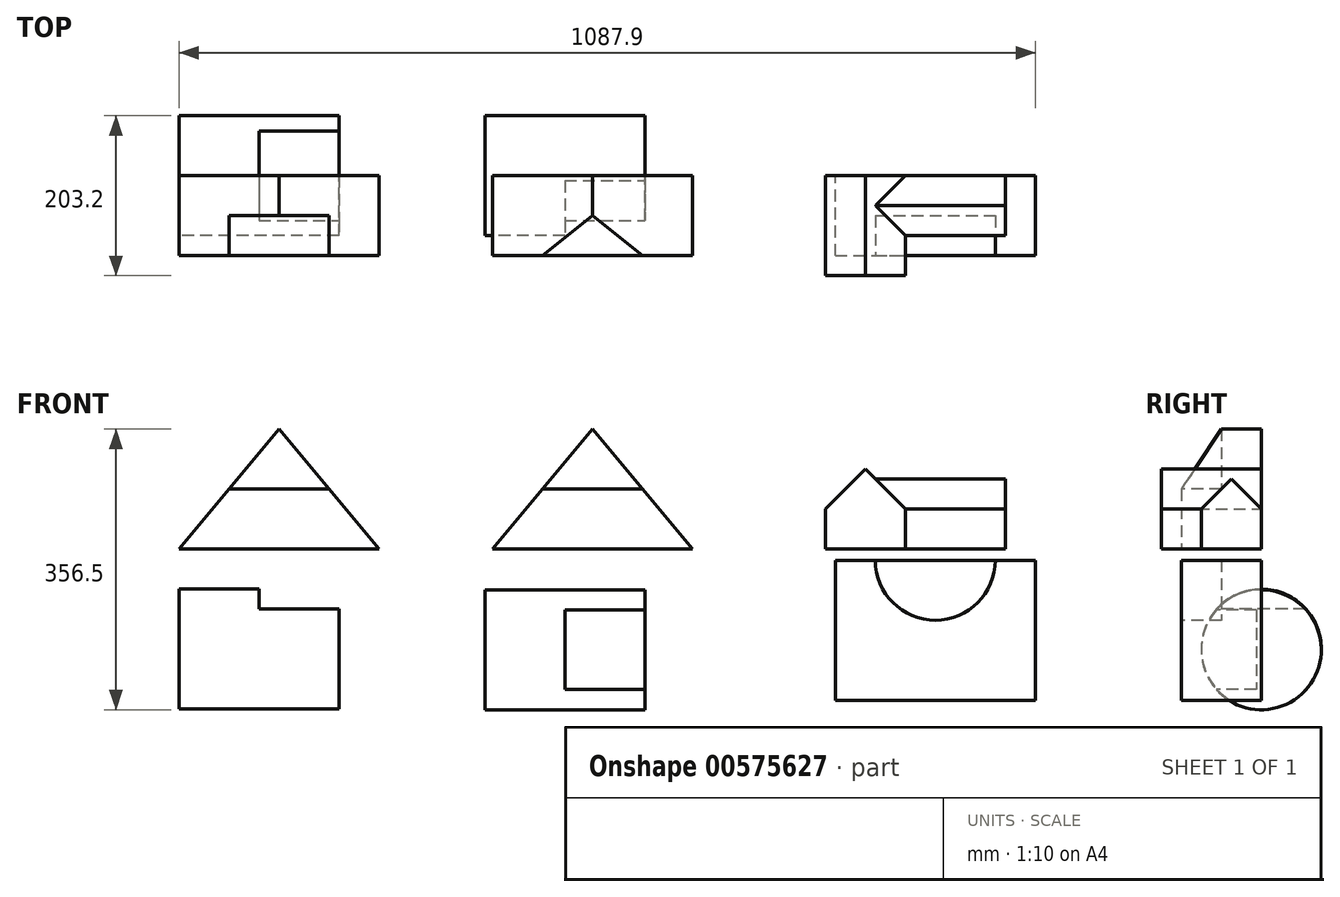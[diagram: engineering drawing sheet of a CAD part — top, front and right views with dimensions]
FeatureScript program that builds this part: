
annotation { "Feature Type Name" : "Feature", "Feature Type Description" : "" }
export const myFeature = defineFeature(function(context is Context, id is Id, definition is map)
    precondition{}
    {
        {
            var Q0;
            Q0=qCreatedBy(makeId("Front.planeOp"),FACE);
            var sketch = newSketch(context, id + "F0", { "sketchPlane" : qUnion([Q0])});
            skLineSegment(sketch, "E0", {"start": v(0, 0) * mm, "end": v(254, 0) * mm});
            skLineSegment(sketch, "E1", {"start": v(127, 152.4) * mm, "end": v(0, 0) * mm});
            skLineSegment(sketch, "E2", {"start": v(127, 152.4) * mm, "end": v(254, 0) * mm});
            skLineSegment(sketch, "E3", {"start": v(127, 76.2) * mm, "end": v(63.5, 76.2) * mm});
            skLineSegment(sketch, "E4", {"start": v(127, 76.2) * mm, "end": v(190.5, 76.2) * mm});
            skSolve(sketch);
        }
        {
            var Q0;
            Q0 = qSketchRegion(id + "F0", true);
            extrude(context, id + "F1", {"entities" : qUnion([Q0]), "depth" : 101.6 * mm, "offsetDistance" : 25.4 * mm});
        }
        {
            var Q0;
            Q0=makeQuery(id+"F1.opExtrude","CAP_FACE",FACE,{"disambiguationData":[OSD([sQuery(id+"F0.wireOp",EDGE,"E0"),sQuery(id+"F0.wireOp",EDGE,"E1"),sQuery(id+"F0.wireOp",EDGE,"E2")])],"isStart":false});
            var sketch = newSketch(context, id + "F2", { "sketchPlane" : qUnion([Q0])});
            skLineSegment(sketch, "E5", {"start": v(127, 76.2) * mm, "end": v(190.5, 76.2) * mm});
            skLineSegment(sketch, "E6", {"start": v(127, 76.2) * mm, "end": v(63.5, 76.2) * mm});
            skSolve(sketch);
        }
        {
            var Q0;
            {var subQ0=sQuery(id+"F2.wireOp",EDGE,"E5");Q0=makeQuery(id+"F2.imprint","IMPRINT",FACE,{"disambiguationData":[TD([[makeQuery(id+"F2.imprint","IMPRINT",EDGE,{"derivedFrom":subQ0}),1.0]])]});}
            extrude(context, id + "F3", {"entities" : qUnion([Q0]), "operationType" : NewBodyOperationType.REMOVE, "oppositeDirection" : true, "depth" : 50.8 * mm, "offsetDistance" : 25.4 * mm});
        }
        {
            var Q0;
            Q0=qCreatedBy(makeId("Front.planeOp"),FACE);
            var sketch = newSketch(context, id + "F4", { "sketchPlane" : qUnion([Q0])});
            skLineSegment(sketch, "E7", {"start": v(398.21, 0) * mm, "end": v(652.21, 0) * mm});
            skLineSegment(sketch, "E8", {"start": v(525.21, 152.4) * mm, "end": v(398.21, 0) * mm});
            skLineSegment(sketch, "E9", {"start": v(525.21, 152.4) * mm, "end": v(652.21, 0) * mm});
            skSolve(sketch);
        }
        {
            var Q0;
            Q0 = qSketchRegion(id + "F4", true);
            extrude(context, id + "F5", {"entities" : qUnion([Q0]), "depth" : 101.6 * mm, "offsetDistance" : 25.4 * mm});
        }
        {
            var Q0;
            Q0=makeQuery(id+"F5.opExtrude","SWEPT_FACE",FACE,{"disambiguationData":[OSD([sQuery(id+"F4.wireOp",EDGE,"E9")])]});
            var sketch = newSketch(context, id + "F6", { "sketchPlane" : qUnion([Q0])});
            skLineSegment(sketch, "E10", {"start": v(-101.6, -318.34) * mm, "end": v(0, -318.34) * mm});
            skLineSegment(sketch, "E11", {"start": v(0, -219.15) * mm, "end": v(-50.8, -219.15) * mm});
            skLineSegment(sketch, "E12", {"start": v(-101.6, -318.34) * mm, "end": v(-50.8, -219.15) * mm});
            skSolve(sketch);
        }
        {
            var Q0;
            {var subQ0=sQuery(id+"F6.wireOp",EDGE,"E12");Q0=makeQuery(id+"F6.imprint","IMPRINT",FACE,{"disambiguationData":[TD([[makeQuery(id+"F6.imprint","IMPRINT",EDGE,{"derivedFrom":subQ0}),1.0]])]});}
            extrude(context, id + "F7", {"entities" : qUnion([Q0]), "operationType" : NewBodyOperationType.REMOVE, "depth" : 101.6 * mm, "offsetDistance" : 25.4 * mm});
        }
        {
            var Q0;
            Q0=makeQuery(id+"F5.opExtrude","CAP_EDGE",EDGE,{"disambiguationData":[OSD([sQuery(id+"F4.wireOp",EDGE,"E7")])],"isStart":false});
            cPoint(context, id + "F8", {"entities" : qUnion([Q0]), "parameter" : 0.5});
        }
        {
            var Q0;
            Q0=makeQuery(id+"F5.opExtrude","CAP_VERTEX",VERTEX,{"disambiguationData":[OSD([sQuery(id+"F4.wireOp",EDGE,"E8"),sQuery(id+"F4.wireOp",EDGE,"E9")])],"isStart":false});
            var Q1;
            Q1=makeQuery(id+"F5.opExtrude","CAP_VERTEX",VERTEX,{"disambiguationData":[OSD([sQuery(id+"F4.wireOp",EDGE,"E8"),sQuery(id+"F4.wireOp",EDGE,"E9")])],"isStart":true});
            var Q2;
            Q2 = qCreatedBy(id + "F8" ,VERTEX);
            cPlane(context, id + "F9", {"entities" : qUnion([Q0, Q1, Q2]), "cplaneType" : CPlaneType.THREE_POINT, "offset" : 25.4 * mm, "width" : 152.4 * mm, "height" : 152.4 * mm});
        }
        {
            var Q0;
            Q0=qCreatedBy(id+"F9.planeOp",FACE);
            var sketch = newSketch(context, id + "F10", { "sketchPlane" : qUnion([Q0])});
            skLineSegment(sketch, "E13", {"start": v(-101.6, 152.4) * mm, "end": v(-50.8, 152.4) * mm});
            skLineSegment(sketch, "E14", {"start": v(-101.6, 152.4) * mm, "end": v(-101.6, 76.2) * mm});
            skLineSegment(sketch, "E15", {"start": v(-101.6, 76.2) * mm, "end": v(-50.8, 152.4) * mm});
            skSolve(sketch);
        }
        {
            var Q0;
            Q0 = qSketchRegion(id + "F10", true);
            extrude(context, id + "F11", {"entities" : qUnion([Q0]), "operationType" : NewBodyOperationType.REMOVE, "endBound" : BoundingType.SYMMETRIC, "depth" : 127 * mm, "offsetDistance" : 25.4 * mm});
        }
        {
            var Q0;
            Q0=qCreatedBy(makeId("Front.planeOp"),FACE);
            var sketch = newSketch(context, id + "F12", { "sketchPlane" : qUnion([Q0])});
            skLineSegment(sketch, "E16", {"start": v(923, 0) * mm, "end": v(821.4, 0) * mm});
            skLineSegment(sketch, "E17", {"start": v(923, 0) * mm, "end": v(923, 50.8) * mm});
            skLineSegment(sketch, "E18", {"start": v(821.4, 0) * mm, "end": v(821.4, 50.8) * mm});
            skLineSegment(sketch, "E19", {"start": v(872.2, 101.6) * mm, "end": v(821.4, 50.8) * mm});
            skLineSegment(sketch, "E20", {"start": v(872.2, 101.6) * mm, "end": v(923, 50.8) * mm});
            skLineSegment(sketch, "E21", {"start": v(923, 0) * mm, "end": v(1050, 0) * mm});
            skLineSegment(sketch, "E22", {"start": v(1050, 0) * mm, "end": v(1050, 50.8) * mm});
            skLineSegment(sketch, "E23", {"start": v(1050, 50.8) * mm, "end": v(923, 50.8) * mm});
            skSolve(sketch);
        }
        {
            var Q0;
            Q0=makeQuery(id+"F12.imprint","IMPRINT",FACE,{"disambiguationData":[TD([[makeQuery(id+"F12.imprint","IMPRINT",EDGE,{"derivedFrom":sQuery(id+"F12.wireOp",EDGE,"E16")}),-1.0]])]});
            var Q1;
            Q1=makeQuery(id+"F12.imprint","IMPRINT",FACE,{"disambiguationData":[TD([[makeQuery(id+"F12.imprint","IMPRINT",EDGE,{"derivedFrom":sQuery(id+"F12.wireOp",EDGE,"E17")}),-1.0]])]});
            extrude(context, id + "F13", {"entities" : qUnion([Q0, Q1]), "depth" : 127 * mm, "offsetDistance" : 25.4 * mm});
        }
        {
            var Q0;
            Q0=makeQuery(id+"F13.opExtrude","SWEPT_FACE",FACE,{"disambiguationData":[OSD([sQuery(id+"F12.wireOp",EDGE,"E22")])]});
            var sketch = newSketch(context, id + "F14", { "sketchPlane" : qUnion([Q0])});
            skLineSegment(sketch, "E24.bottom", {"start": v(-127, 50.8) * mm, "end": v(-76.2, 50.8) * mm});
            skLineSegment(sketch, "E24.top", {"start": v(-127, 0) * mm, "end": v(-76.2, 0) * mm});
            skLineSegment(sketch, "E24.left", {"start": v(-127, 50.8) * mm, "end": v(-127, 0) * mm});
            skLineSegment(sketch, "E24.right", {"start": v(-76.2, 50.8) * mm, "end": v(-76.2, 0) * mm});
            skLineSegment(sketch, "E25", {"start": v(-76.2, 0) * mm, "end": v(0, 0) * mm});
            skLineSegment(sketch, "E26", {"start": v(-38.1, 88.9) * mm, "end": v(-76.2, 50.8) * mm});
            skLineSegment(sketch, "E27", {"start": v(-38.1, 88.9) * mm, "end": v(0, 50.8) * mm});
            skLineSegment(sketch, "E28", {"start": v(-127, 50.8) * mm, "end": v(-127, 88.44) * mm});
            skLineSegment(sketch, "E29", {"start": v(-127, 88.44) * mm, "end": v(-38.1, 88.9) * mm});
            skLineSegment(sketch, "E30", {"start": v(-38.1, 88.9) * mm, "end": v(0, 89.1) * mm});
            skSolve(sketch);
        }
        {
            var Q0;
            {var subQ0=sQuery(id+"F14.wireOp",EDGE,"E26");Q0=makeQuery(id+"F14.imprint","IMPRINT",FACE,{"disambiguationData":[TD([[makeQuery(id+"F14.imprint","IMPRINT",EDGE,{"derivedFrom":subQ0}),1.0]])]});}
            extrude(context, id + "F15", {"entities" : qUnion([Q0]), "operationType" : NewBodyOperationType.ADD, "oppositeDirection" : true, "depth" : 164.34 * mm, "offsetDistance" : 25.4 * mm});
        }
        {
            var Q0;
            Q0=makeQuery(id+"F13.opExtrude","CAP_FACE",FACE,{"disambiguationData":[OSD([sQuery(id+"F12.wireOp",EDGE,"E16"),sQuery(id+"F12.wireOp",EDGE,"E18"),sQuery(id+"F12.wireOp",EDGE,"E19"),sQuery(id+"F12.wireOp",EDGE,"E20"),sQuery(id+"F12.wireOp",EDGE,"E21"),sQuery(id+"F12.wireOp",EDGE,"E22"),sQuery(id+"F12.wireOp",EDGE,"E23")])],"isStart":false});
            var sketch = newSketch(context, id + "F16", { "sketchPlane" : qUnion([Q0])});
            skLineSegment(sketch, "E31.bottom", {"start": v(1050, 0) * mm, "end": v(923, 0) * mm});
            skLineSegment(sketch, "E31.top", {"start": v(1050, 50.8) * mm, "end": v(923, 50.8) * mm});
            skLineSegment(sketch, "E31.left", {"start": v(1050, 0) * mm, "end": v(1050, 50.8) * mm});
            skLineSegment(sketch, "E31.right", {"start": v(923, 0) * mm, "end": v(923, 50.8) * mm});
            skSolve(sketch);
        }
        {
            var Q0;
            Q0=makeQuery(id+"F16.imprint","IMPRINT",FACE,{"disambiguationData":[TD([[makeQuery(id+"F16.imprint","IMPRINT",EDGE,{"derivedFrom":sQuery(id+"F16.wireOp",EDGE,"E31.bottom")}),-1.0]])]});
            extrude(context, id + "F17", {"entities" : qUnion([Q0]), "operationType" : NewBodyOperationType.REMOVE, "oppositeDirection" : true, "depth" : 50.8 * mm, "offsetDistance" : 25.4 * mm});
        }
        {
            var Q0;
            Q0=qCreatedBy(makeId("Right.planeOp"),FACE);
            var sketch = newSketch(context, id + "F18", { "sketchPlane" : qUnion([Q0])});
            skCircle(sketch, "E32", {"center": v(0, -127) * mm, "radius": 76.2 * mm});
            skSolve(sketch);
        }
        {
            var Q0;
            Q0 = qSketchRegion(id + "F18", true);
            extrude(context, id + "F19", {"entities" : qUnion([Q0]), "depth" : 203.2 * mm, "offsetDistance" : 25.4 * mm});
        }
        {
            var Q0;
            Q0=makeQuery(id+"F19.opExtrude","CAP_FACE",FACE,{"disambiguationData":[OSD([sQuery(id+"F18.wireOp",EDGE,"E32")])],"isStart":false});
            var sketch = newSketch(context, id + "F20", { "sketchPlane" : qUnion([Q0])});
            skLineSegment(sketch, "E33", {"start": v(0, -203.2) * mm, "end": v(0, -76.2) * mm});
            skLineSegment(sketch, "E34", {"start": v(0, -76.2) * mm, "end": v(56.8, -76.2) * mm});
            skLineSegment(sketch, "E35", {"start": v(0, -76.2) * mm, "end": v(-56.8, -76.2) * mm});
            skLineSegment(sketch, "E36", {"start": v(0, -76.2) * mm, "end": v(0, -50.8) * mm});
            skSolve(sketch);
        }
        {
            var Q0;
            {var subQ0=sQuery(id+"F20.wireOp",EDGE,"E35");Q0=makeQuery(id+"F20.imprint","IMPRINT",FACE,{"disambiguationData":[TD([[makeQuery(id+"F20.imprint","IMPRINT",EDGE,{"derivedFrom":subQ0}),-1.0]])]});}
            var Q1;
            {var subQ0=sQuery(id+"F20.wireOp",EDGE,"E34");Q1=makeQuery(id+"F20.imprint","IMPRINT",FACE,{"disambiguationData":[TD([[makeQuery(id+"F20.imprint","IMPRINT",EDGE,{"derivedFrom":subQ0}),1.0]])]});}
            extrude(context, id + "F21", {"entities" : qUnion([Q0, Q1]), "operationType" : NewBodyOperationType.REMOVE, "oppositeDirection" : true, "depth" : 101.6 * mm, "offsetDistance" : 25.4 * mm});
        }
        {
            var Q0;
            Q0=qCreatedBy(makeId("Right.planeOp"),FACE);
            cPlane(context, id + "F22", {"entities" : qUnion([Q0]), "cplaneType" : CPlaneType.OFFSET, "offset" : 388.62 * mm, "width" : 152.4 * mm, "height" : 152.4 * mm});
        }
        {
            var Q0;
            Q0=qCreatedBy(id+"F22.planeOp",FACE);
            var sketch = newSketch(context, id + "F23", { "sketchPlane" : qUnion([Q0])});
            skCircle(sketch, "E37", {"center": v(0, -127.9) * mm, "radius": 76.2 * mm});
            skSolve(sketch);
        }
        {
            var Q0;
            Q0 = qSketchRegion(id + "F23", true);
            extrude(context, id + "F24", {"entities" : qUnion([Q0]), "depth" : 203.2 * mm, "offsetDistance" : 25.4 * mm});
        }
        {
            var Q0;
            Q0=makeQuery(id+"F24.opExtrude","CAP_FACE",FACE,{"disambiguationData":[OSD([sQuery(id+"F23.wireOp",EDGE,"E37")])],"isStart":false});
            var sketch = newSketch(context, id + "F25", { "sketchPlane" : qUnion([Q0])});
            skLineSegment(sketch, "E38", {"start": v(-6.22, -203.85) * mm, "end": v(-6.22, -178.45) * mm});
            skLineSegment(sketch, "E39", {"start": v(-6.22, -178.45) * mm, "end": v(-57.02, -178.45) * mm});
            skLineSegment(sketch, "E40", {"start": v(-6.22, -51.96) * mm, "end": v(-6.22, -77.36) * mm});
            skLineSegment(sketch, "E41", {"start": v(-6.22, -77.36) * mm, "end": v(-57.02, -77.36) * mm});
            skLineSegment(sketch, "E42", {"start": v(-6.22, -77.36) * mm, "end": v(-6.22, -178.45) * mm});
            skSolve(sketch);
        }
        {
            var Q0;
            {var subQ0=sQuery(id+"F25.wireOp",EDGE,"E39");Q0=makeQuery(id+"F25.imprint","IMPRINT",FACE,{"disambiguationData":[TD([[makeQuery(id+"F25.imprint","IMPRINT",EDGE,{"derivedFrom":subQ0}),-1.0]])]});}
            extrude(context, id + "F26", {"entities" : qUnion([Q0]), "operationType" : NewBodyOperationType.REMOVE, "oppositeDirection" : true, "depth" : 101.6 * mm, "offsetDistance" : 25.4 * mm});
        }
        {
            var Q0;
            Q0=qCreatedBy(makeId("Front.planeOp"),FACE);
            var sketch = newSketch(context, id + "F27", { "sketchPlane" : qUnion([Q0])});
            skLineSegment(sketch, "E43", {"start": v(833.9, -191.92) * mm, "end": v(1087.9, -191.92) * mm});
            skLineSegment(sketch, "E44", {"start": v(1087.9, -191.92) * mm, "end": v(1087.9, -14.12) * mm});
            skLineSegment(sketch, "E45", {"start": v(833.9, -191.92) * mm, "end": v(833.9, -14.12) * mm});
            skLineSegment(sketch, "E46", {"start": v(833.9, -14.12) * mm, "end": v(1087.9, -14.12) * mm});
            skSolve(sketch);
        }
        {
            var Q0;
            Q0=makeQuery(id+"F27.imprint","IMPRINT",FACE,{"disambiguationData":[TD([[makeQuery(id+"F27.imprint","IMPRINT",EDGE,{"derivedFrom":sQuery(id+"F27.wireOp",EDGE,"E43")}),1.0]])]});
            extrude(context, id + "F28", {"entities" : qUnion([Q0]), "depth" : 101.6 * mm, "offsetDistance" : 25.4 * mm});
        }
        {
            var Q0;
            Q0=makeQuery(id+"F28.opExtrude","CAP_FACE",FACE,{"disambiguationData":[OSD([sQuery(id+"F27.wireOp",EDGE,"E43"),sQuery(id+"F27.wireOp",EDGE,"E44"),sQuery(id+"F27.wireOp",EDGE,"E45"),sQuery(id+"F27.wireOp",EDGE,"E46")])],"isStart":false});
            var sketch = newSketch(context, id + "F29", { "sketchPlane" : qUnion([Q0])});
            skCircle(sketch, "E47", {"center": v(960.9, -14.12) * mm, "radius": 76.2 * mm});
            skSolve(sketch);
        }
        {
            var Q0;
            {var subQ0=sQuery(id+"F29.wireOp",EDGE,"E47");var subQ1=makeQuery(id+"F28.opExtrude","CAP_EDGE",EDGE,{"disambiguationData":[OSD([sQuery(id+"F27.wireOp",EDGE,"E46")])],"isStart":false});var subQ2=makeQuery(id+"F29.imprint","INTERSECT",VERTEX,{"disambiguationData":[OD(0.0)],"derivedFrom":[subQ1,subQ0]});Q0=makeQuery(id+"F29.imprint","IMPRINT",FACE,{"disambiguationData":[TD([[makeQuery(id+"F29.imprint","IMPRINT",EDGE,{"disambiguationData":[TD([[subQ2,1.0]])],"derivedFrom":subQ0}),1.0]])]});}
            extrude(context, id + "F30", {"entities" : qUnion([Q0]), "operationType" : NewBodyOperationType.REMOVE, "oppositeDirection" : true, "depth" : 50.8 * mm, "offsetDistance" : 25.4 * mm});
        }
    });
